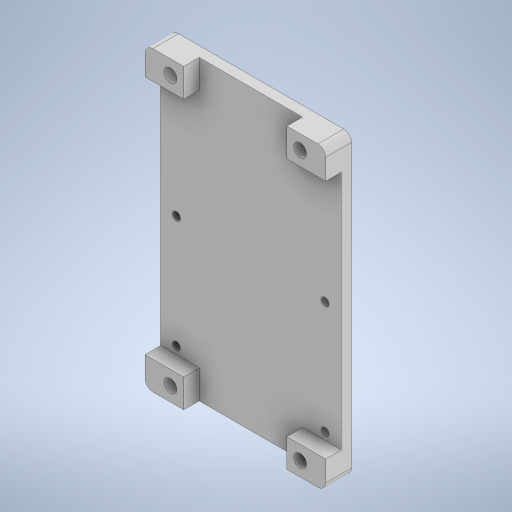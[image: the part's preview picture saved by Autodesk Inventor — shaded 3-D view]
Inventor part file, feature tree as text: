
AUTODESK INVENTOR PART (.ipt)
format: ipt  version: 2023 (Build 270158000, 158)  size: 324,608 bytes
history: native  units: mm
features: sketch x4, extrude x4, other x1, hole x1
ambient origin geometry x8: Origin, YZ Plane, XZ Plane, XY Plane, X Axis, Y Axis, Z Axis, Center Point
bodies: Body1 (feature_tree)
feature tree (10):
  other  "솔리드1"
  sketch  "스케치1"
  extrude  "돌출1"  Depth=35.0mm
  extrude  "돌출2"  Depth=57.6mm
  hole  "구멍1"  [1 undecoded]
  extrude  "돌출3"  Depth=52.1mm
  extrude  "돌출4"  Depth=2.5mm
  sketch  "스케치3"
  sketch  "스케치4"
  sketch  "스케치5"
note: 1 required parameter value undecoded (feature->parameter linkage not recoverable at this tier; creation-order binding heuristic only, values carry confidence <= 0.55)
